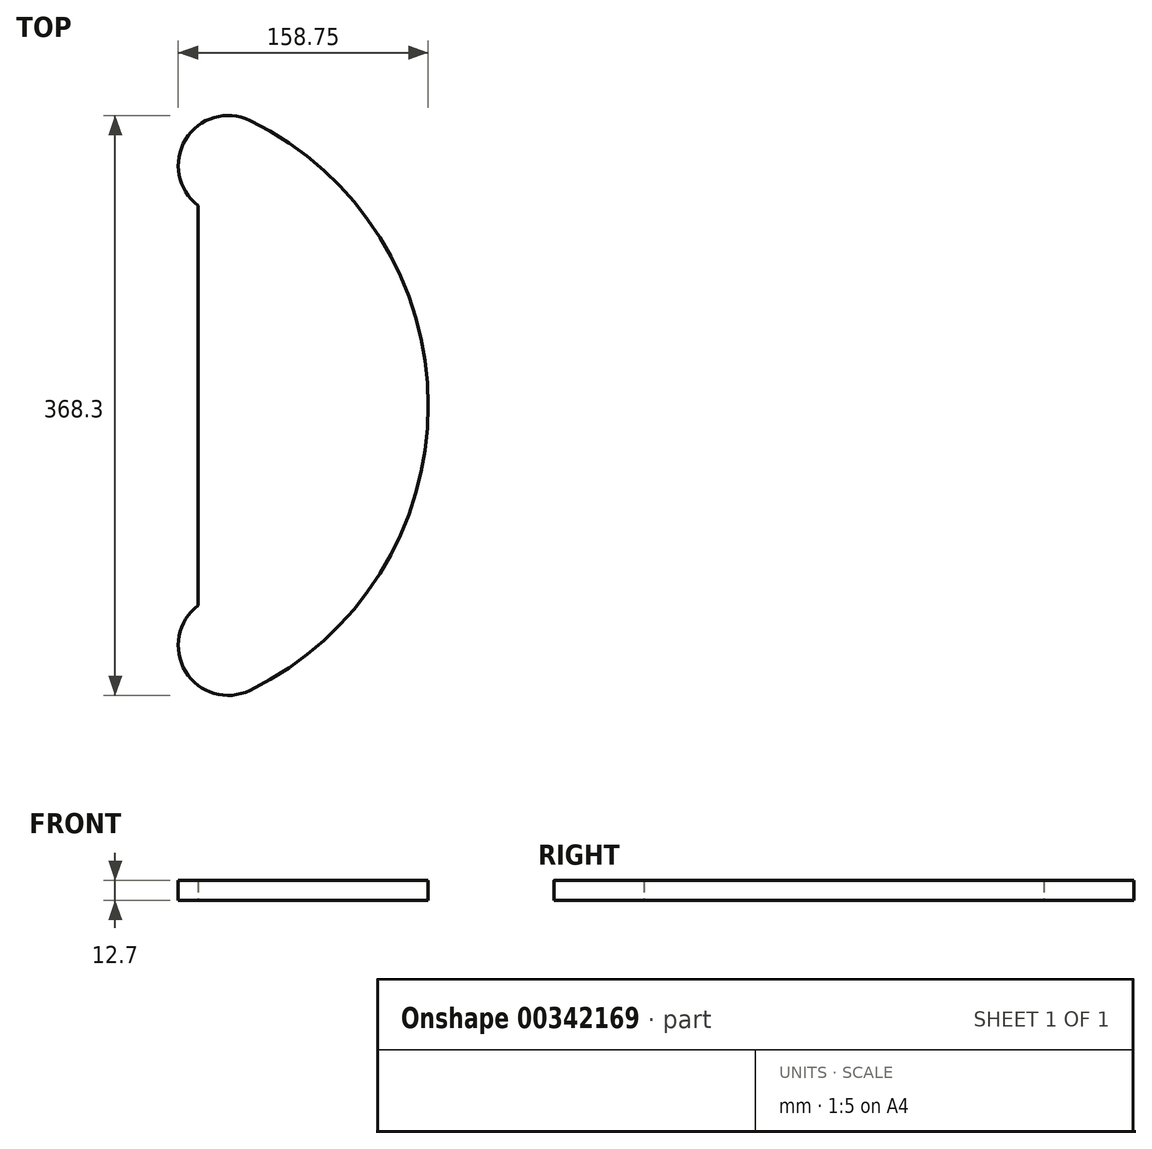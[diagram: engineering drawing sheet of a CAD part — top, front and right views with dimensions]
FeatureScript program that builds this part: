
annotation { "Feature Type Name" : "Feature", "Feature Type Description" : "" }
export const myFeature = defineFeature(function(context is Context, id is Id, definition is map)
    precondition{}
    {
        {
            var Q0;
            Q0=qCreatedBy(makeId("Top.planeOp"),FACE);
            var sketch = newSketch(context, id + "F0", { "sketchPlane" : qUnion([Q0])});
            skArc(sketch, "E0", {"start": v(13.91, 180.94) * mm, "mid": v(-27.1, 168.96) * mm, "end": v(-19.05, 127) * mm});
            skArc(sketch, "E1.MirrorC", {"start": v(13.91, -180.94) * mm, "mid": v(-27.1, -168.96) * mm, "end": v(-19.05, -127) * mm});
            skArc(sketch, "E2", {"start": v(13.91, -180.94) * mm, "mid": v(127, 0) * mm, "end": v(13.91, 180.94) * mm});
            skLineSegment(sketch, "E3", {"start": v(-19.05, 127) * mm, "end": v(-19.05, -127) * mm});
            skSolve(sketch);
        }
        {
            var Q0;
            Q0=makeQuery(id+"F0.imprint","IMPRINT",FACE,{"disambiguationData":[TD([[makeQuery(id+"F0.imprint","IMPRINT",EDGE,{"derivedFrom":sQuery(id+"F0.wireOp",EDGE,"E0")}),1.0]])]});
            extrude(context, id + "F1", {"entities" : qUnion([Q0]), "depth" : 12.7 * mm});
        }
    });
